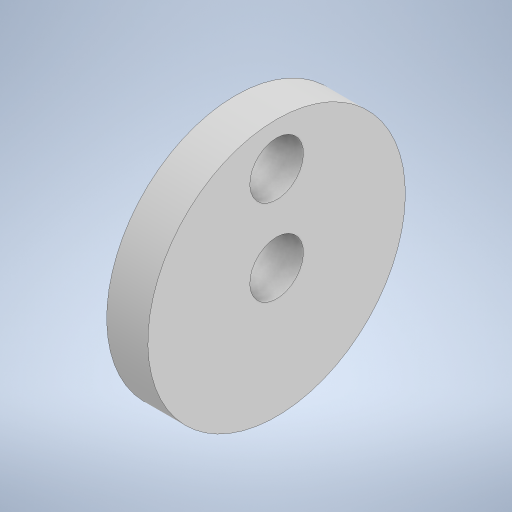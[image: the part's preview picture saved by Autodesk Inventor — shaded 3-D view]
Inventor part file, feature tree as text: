
AUTODESK INVENTOR PART (.ipt)
format: ipt  version: 2023 (Build 270158000, 158)  size: 236,544 bytes
history: native  units: in
note: dims shown in document units (in); Inventor stores cm internally (conversion verified against a paired STEP export)
features: extrude x1, sketch x1
ambient origin geometry x8: Origin, YZ Plane, XZ Plane, XY Plane, X Axis, Y Axis, Z Axis, Center Point
bodies: Solid1 (feature_tree)
feature tree (2):
  extrude  "Extrusion1"  Depth=0.06in
  sketch  "Sketch1"  dims[d0=0.375in d1=0.0781in d2=0.125in d3=0.0781in d4=0.06in d5=0.0in]
